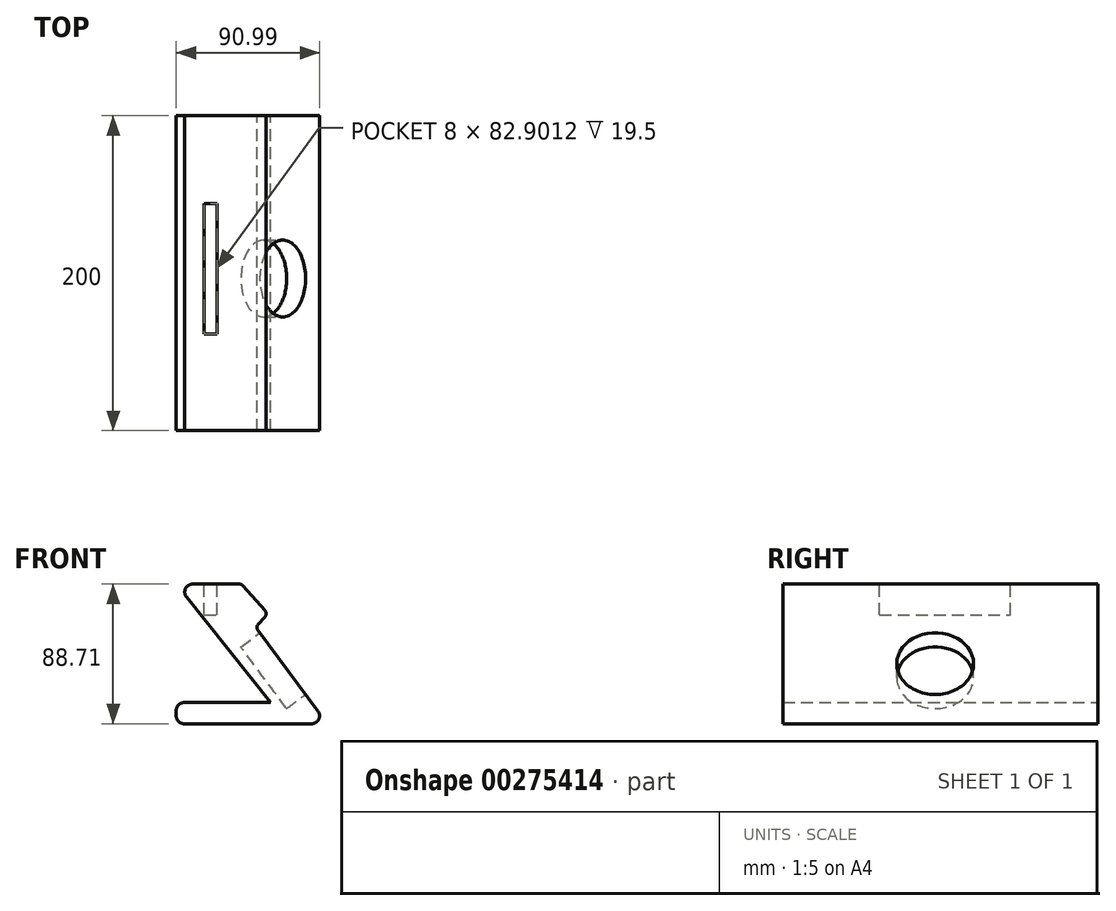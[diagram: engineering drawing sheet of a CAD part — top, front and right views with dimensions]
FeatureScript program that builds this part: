
annotation { "Feature Type Name" : "Feature", "Feature Type Description" : "" }
export const myFeature = defineFeature(function(context is Context, id is Id, definition is map)
    precondition{}
    {
        {
            var Q0;
            Q0=qCreatedBy(makeId("Front.planeOp"),FACE);
            var sketch = newSketch(context, id + "F0", { "sketchPlane" : qUnion([Q0])});
            skLineSegment(sketch, "E0.bottom", {"start": v(-12.37, 45.3) * mm, "end": v(0, 45.3) * mm});
            skLineSegment(sketch, "E0.left", {"start": v(-22.75, -29.92) * mm, "end": v(-22.75, -43.4) * mm});
            skLineSegment(sketch, "E1", {"start": v(-16.27, 37.19) * mm, "end": v(37.25, -29.92) * mm});
            skLineSegment(sketch, "E2", {"start": v(37.25, -29.92) * mm, "end": v(-17.75, -29.92) * mm});
            skLineSegment(sketch, "E3", {"start": v(-22.75, -34.92) * mm, "end": v(-22.75, -38.4) * mm});
            skLineSegment(sketch, "E4", {"start": v(-17.75, -43.4) * mm, "end": v(63.24, -43.4) * mm});
            skPoint(sketch, "E5.end.orphan", {"position": v(0, 45.3) * mm});
            skPoint(sketch, "E6.visualSharp", {"position": v(72.78, -43.4) * mm});
            skArc(sketch, "E6.filletArc", {"start": v(63.24, -43.4) * mm, "mid": v(67.7, -40.65) * mm, "end": v(67.25, -35.42) * mm});
            skPoint(sketch, "E7.visualSharp", {"position": v(-22.75, -43.4) * mm});
            skArc(sketch, "E7.filletArc", {"start": v(-22.75, -38.4) * mm, "mid": v(-21.28, -41.94) * mm, "end": v(-17.75, -43.4) * mm});
            skPoint(sketch, "E8.visualSharp", {"position": v(-22.75, -29.92) * mm});
            skArc(sketch, "E8.filletArc", {"start": v(-17.75, -29.92) * mm, "mid": v(-21.28, -31.38) * mm, "end": v(-22.75, -34.92) * mm});
            skLineSegment(sketch, "E9", {"start": v(67.25, -35.42) * mm, "end": v(29.07, 16.03) * mm});
            skPoint(sketch, "E10.visualSharp", {"position": v(-22.75, 45.3) * mm});
            skArc(sketch, "E10.filletArc", {"start": v(-12.37, 45.3) * mm, "mid": v(-16.87, 42.48) * mm, "end": v(-16.27, 37.19) * mm});
            skLineSegment(sketch, "E11", {"start": v(0, 45.3) * mm, "end": v(17.38, 45.3) * mm});
            skLineSegment(sketch, "E12", {"start": v(19.62, 44.3) * mm, "end": v(33.59, 28.56) * mm});
            skLineSegment(sketch, "E13", {"start": v(33.56, 24.54) * mm, "end": v(29.27, 19.84) * mm});
            skPoint(sketch, "E14.visualSharp", {"position": v(18.73, 45.3) * mm});
            skArc(sketch, "E14.filletArc", {"start": v(19.62, 44.3) * mm, "mid": v(18.6, 45.04) * mm, "end": v(17.38, 45.3) * mm});
            skPoint(sketch, "E15.visualSharp", {"position": v(35.38, 26.54) * mm});
            skArc(sketch, "E15.filletArc", {"start": v(33.56, 24.54) * mm, "mid": v(34.34, 26.54) * mm, "end": v(33.59, 28.56) * mm});
            skPoint(sketch, "E16.visualSharp", {"position": v(27.6, 18.01) * mm});
            skArc(sketch, "E16.filletArc", {"start": v(29.27, 19.84) * mm, "mid": v(28.49, 17.97) * mm, "end": v(29.07, 16.03) * mm});
            skSolve(sketch);
        }
        {
            var Q0;
            Q0 = qSketchRegion(id + "F0", true);
            extrude(context, id + "F1", {"entities" : qUnion([Q0]), "depth" : 200 * mm});
        }
        {
            var Q0;
            Q0=makeQuery(id+"F1.opExtrude","SWEPT_FACE",FACE,{"disambiguationData":[OSD([sQuery(id+"F0.wireOp",EDGE,"E0.bottom"),sQuery(id+"F0.wireOp",EDGE,"E11")])]});
            var sketch = newSketch(context, id + "F2", { "sketchPlane" : qUnion([Q0])});
            skLineSegment(sketch, "E17.bottom", {"start": v(-4.98, -138.64) * mm, "end": v(3.02, -138.64) * mm});
            skLineSegment(sketch, "E17.top", {"start": v(-4.98, -55.74) * mm, "end": v(3.02, -55.74) * mm});
            skLineSegment(sketch, "E17.left", {"start": v(-4.98, -138.64) * mm, "end": v(-4.98, -55.74) * mm});
            skLineSegment(sketch, "E17.right", {"start": v(3.02, -138.64) * mm, "end": v(3.02, -55.74) * mm});
            skSolve(sketch);
        }
        {
            var Q0;
            Q0=makeQuery(id+"F2.imprint","IMPRINT",FACE,{"disambiguationData":[TD([[makeQuery(id+"F2.imprint","IMPRINT",EDGE,{"derivedFrom":sQuery(id+"F2.wireOp",EDGE,"E17.bottom")}),1.0]])]});
            extrude(context, id + "F3", {"entities" : qUnion([Q0]), "operationType" : NewBodyOperationType.REMOVE, "oppositeDirection" : true, "depth" : 19.5 * mm});
        }
        {
            var Q0;
            Q0=makeQuery(id+"F1.opExtrude","SWEPT_FACE",FACE,{"disambiguationData":[OSD([sQuery(id+"F0.wireOp",EDGE,"E9")])]});
            var sketch = newSketch(context, id + "F4", { "sketchPlane" : qUnion([Q0])});
            skCircle(sketch, "E18", {"center": v(-103.38, -30.94) * mm, "radius": 24.4 * mm});
            skSolve(sketch);
        }
        {
            var Q0;
            Q0=makeQuery(id+"F4.imprint","IMPRINT",FACE,{"disambiguationData":[TD([[makeQuery(id+"F4.imprint","IMPRINT",EDGE,{"derivedFrom":sQuery(id+"F4.wireOp",EDGE,"E18")}),1.0]])]});
            extrude(context, id + "F5", {"entities" : qUnion([Q0]), "operationType" : NewBodyOperationType.REMOVE, "oppositeDirection" : true, "depth" : 15 * mm});
        }
    });
